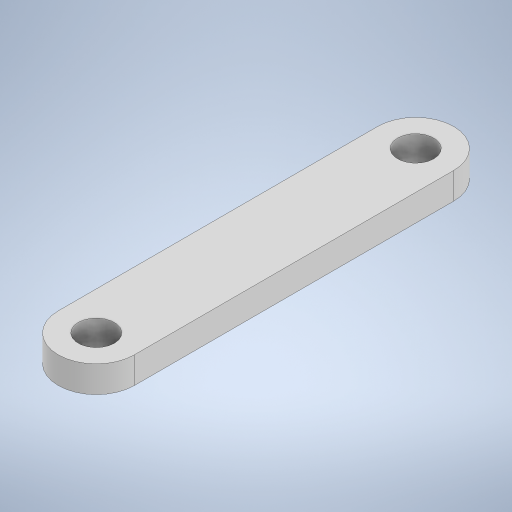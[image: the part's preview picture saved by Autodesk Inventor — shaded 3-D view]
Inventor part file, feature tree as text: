
AUTODESK INVENTOR PART (.ipt)
format: ipt  version: 2024 (Build 280153000, 153)  size: 227,840 bytes
history: native  units: in
note: dims shown in document units (in); Inventor stores cm internally (conversion verified against a paired STEP export)
features: extrude x1, sketch x1
ambient origin geometry x8: Origin, YZ Plane, XZ Plane, XY Plane, X Axis, Y Axis, Z Axis, Center Point
bodies: Solid1 (feature_tree)
feature tree (2):
  extrude  "Extrusion1"  Depth=0.125in
  sketch  "Sketch1"  dims[d0=0.17in d1=0.17in d2=1.5in d3=0.0938in d4=0.0938in d5=0.125in d6=0.0in]
